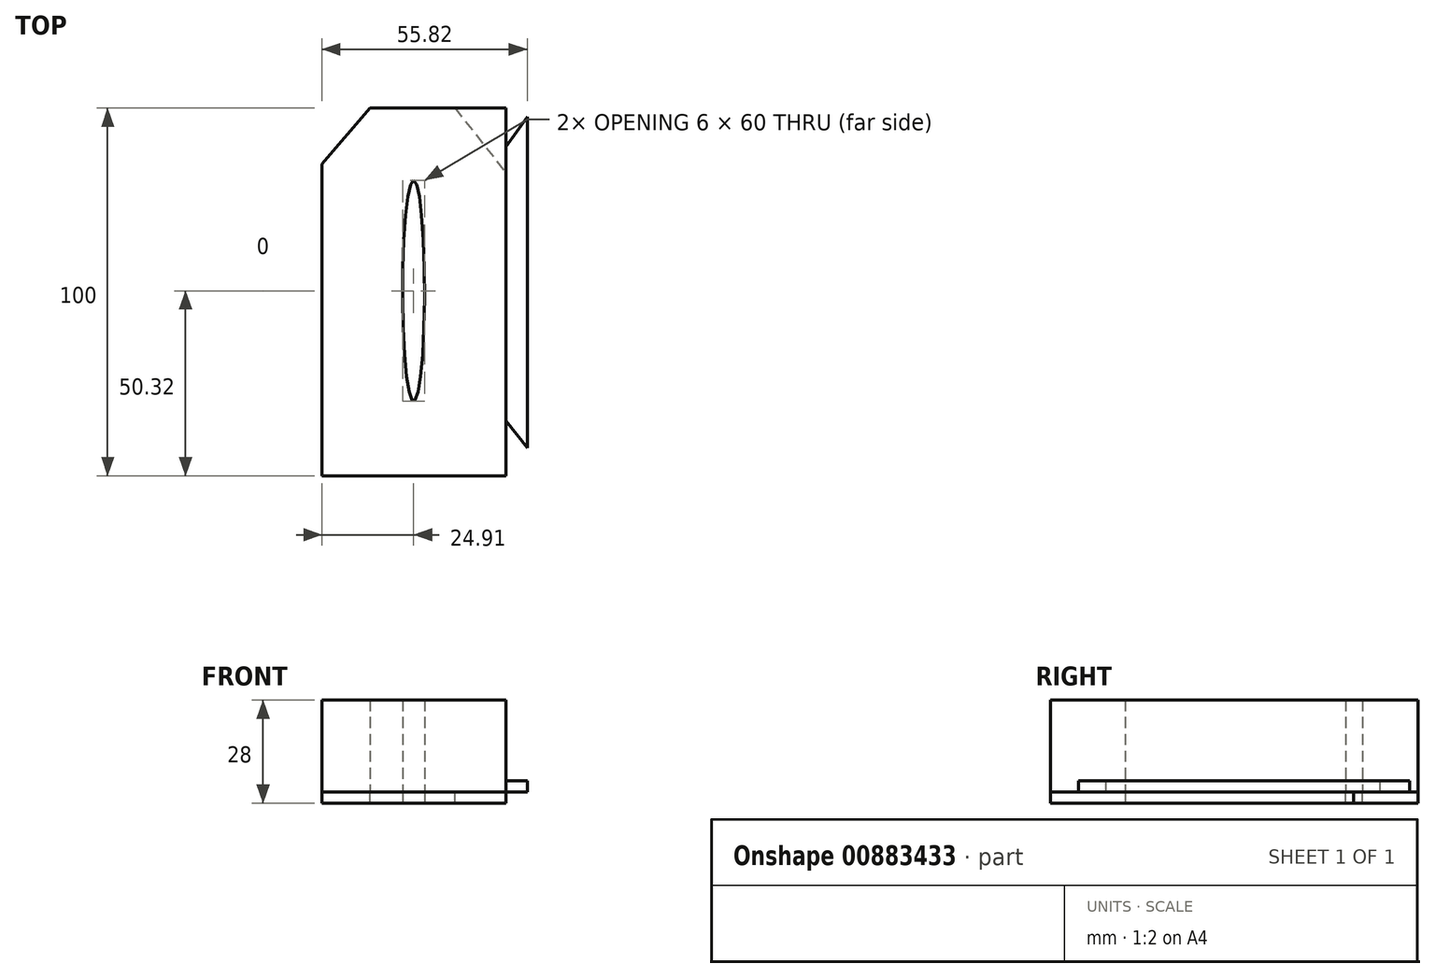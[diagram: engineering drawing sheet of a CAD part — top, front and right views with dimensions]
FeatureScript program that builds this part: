
annotation { "Feature Type Name" : "Feature", "Feature Type Description" : "" }
export const myFeature = defineFeature(function(context is Context, id is Id, definition is map)
    precondition{}
    {
        {
            var Q0;
            Q0=qCreatedBy(makeId("Top.planeOp"),FACE);
            var sketch = newSketch(context, id + "F0", { "sketchPlane" : qUnion([Q0])});
            skLineSegment(sketch, "E0.bottom", {"start": v(-24.91, 49.68) * mm, "end": v(25.09, 49.68) * mm});
            skLineSegment(sketch, "E0.top", {"start": v(-24.91, -50.32) * mm, "end": v(25.09, -50.32) * mm});
            skLineSegment(sketch, "E0.left", {"start": v(-24.91, 49.68) * mm, "end": v(-24.91, -50.32) * mm});
            skLineSegment(sketch, "E0.right", {"start": v(25.09, 49.68) * mm, "end": v(25.09, -50.32) * mm});
            skSolve(sketch);
        }
        {
            var Q0;
            Q0=makeQuery(id+"F0.imprint","IMPRINT",FACE,{"disambiguationData":[TD([[makeQuery(id+"F0.imprint","IMPRINT",EDGE,{"derivedFrom":sQuery(id+"F0.wireOp",EDGE,"E0.bottom")}),-1.0]])]});
            extrude(context, id + "F1", {"entities" : qUnion([Q0]), "depth" : 3 * mm, "offsetDistance" : 25 * mm});
        }
        {
            var Q0;
            Q0=makeQuery(id+"F1.opExtrude","CAP_FACE",FACE,{"disambiguationData":[OSD([sQuery(id+"F0.wireOp",EDGE,"E0.bottom"),sQuery(id+"F0.wireOp",EDGE,"E0.top"),sQuery(id+"F0.wireOp",EDGE,"E0.left"),sQuery(id+"F0.wireOp",EDGE,"E0.right")])],"isStart":false});
            var sketch = newSketch(context, id + "F2", { "sketchPlane" : qUnion([Q0])});
            skLineSegment(sketch, "E1", {"start": v(25.09, 39.2) * mm, "end": v(30.9, 47.34) * mm});
            skLineSegment(sketch, "E2", {"start": v(30.9, 47.34) * mm, "end": v(30.9, -42.66) * mm});
            skLineSegment(sketch, "E3", {"start": v(30.9, -42.66) * mm, "end": v(25.09, -35.3) * mm});
            skSolve(sketch);
        }
        {
            var Q0;
            {var subQ0=sQuery(id+"F2.wireOp",EDGE,"E1");Q0=makeQuery(id+"F2.imprint","IMPRINT",FACE,{"disambiguationData":[TD([[makeQuery(id+"F2.imprint","IMPRINT",EDGE,{"derivedFrom":subQ0}),-1.0]])]});}
            extrude(context, id + "F3", {"entities" : qUnion([Q0]), "depth" : 3 * mm, "offsetDistance" : 25 * mm});
        }
        {
            var Q0;
            Q0=makeQuery(id+"F1.opExtrude","CAP_FACE",FACE,{"disambiguationData":[OSD([sQuery(id+"F0.wireOp",EDGE,"E0.bottom"),sQuery(id+"F0.wireOp",EDGE,"E0.top"),sQuery(id+"F0.wireOp",EDGE,"E0.left"),sQuery(id+"F0.wireOp",EDGE,"E0.right")])],"isStart":false});
            var sketch = newSketch(context, id + "F4", { "sketchPlane" : qUnion([Q0])});
            skLineSegment(sketch, "E4", {"start": v(-24.91, 34.5) * mm, "end": v(-11.88, 49.68) * mm});
            skSolve(sketch);
        }
        {
            var Q0;
            {var subQ2=sQuery(id+"F4.wireOp",EDGE,"E4");Q0=makeQuery(id+"F4.imprint","IMPRINT",FACE,{"disambiguationData":[TD([[makeQuery(id+"F4.imprint","IMPRINT",EDGE,{"derivedFrom":subQ2}),-1.0]])]});}
            var sketch = newSketch(context, id + "F5", { "sketchPlane" : qUnion([Q0])});
            skLineSegment(sketch, "E5", {"start": v(12.58, 49.08) * mm, "end": v(24.3, 34.92) * mm});
            skSolve(sketch);
        }
        {
            var Q0;
            Q0 = qSketchRegion(id + "F4", true);
            var Q1;
            {var subQ0=sQuery(id+"F4.wireOp",EDGE,"E4");Q1=makeQuery(id+"F4.imprint","IMPRINT",FACE,{"disambiguationData":[TD([[makeQuery(id+"F4.imprint","IMPRINT",EDGE,{"derivedFrom":subQ0}),1.0]])]});}
            extrude(context, id + "F6", {"entities" : qUnion([Q0, Q1]), "operationType" : NewBodyOperationType.REMOVE, "oppositeDirection" : true, "depth" : 3 * mm, "offsetDistance" : 25 * mm});
        }
        {
            var Q0;
            {var subQ2=sQuery(id+"F4.wireOp",EDGE,"E4");Q0=makeQuery(id+"F5.imprint","IMPRINT",FACE,{"disambiguationData":[TD([[makeQuery(id+"F5.imprint","IMPRINT",EDGE,{"derivedFrom":makeQuery(id+"F4.imprint","IMPRINT",EDGE,{"derivedFrom":subQ2})}),-1.0]])]});}
            var sketch = newSketch(context, id + "F7", { "sketchPlane" : qUnion([Q0])});
            skLineSegment(sketch, "E6", {"start": v(11.05, 49.93) * mm, "end": v(25.51, 31.56) * mm});
            skSolve(sketch);
        }
        {
            var Q0;
            {var subQ0=sQuery(id+"F7.wireOp",EDGE,"E6");var subQ1=makeQuery(id+"F1.opExtrude","CAP_EDGE",EDGE,{"disambiguationData":[OSD([sQuery(id+"F0.wireOp",EDGE,"E0.right")])],"isStart":false});var subQ2=makeQuery(id+"F5.imprint","IMPRINT",EDGE,{"derivedFrom":makeQuery(id+"F4.imprint","IMPRINT",EDGE,{"derivedFrom":subQ1})});var subQ3=makeQuery(id+"F7.imprint","INTERSECT",VERTEX,{"derivedFrom":[subQ2,subQ0]});Q0=makeQuery(id+"F7.imprint","IMPRINT",FACE,{"disambiguationData":[TD([[makeQuery(id+"F7.imprint","IMPRINT",EDGE,{"disambiguationData":[TD([[subQ3,1.0]])],"derivedFrom":subQ0}),1.0]])]});}
            extrude(context, id + "F8", {"entities" : qUnion([Q0]), "operationType" : NewBodyOperationType.REMOVE, "oppositeDirection" : true, "depth" : 25 * mm, "offsetDistance" : 25 * mm});
        }
        {
            var Q0;
            {var subQ2=sQuery(id+"F4.wireOp",EDGE,"E4");Q0=makeQuery(id+"F5.imprint","IMPRINT",FACE,{"disambiguationData":[TD([[makeQuery(id+"F5.imprint","IMPRINT",EDGE,{"derivedFrom":makeQuery(id+"F4.imprint","IMPRINT",EDGE,{"derivedFrom":subQ2})}),-1.0]])]});}
            var sketch = newSketch(context, id + "F9", { "sketchPlane" : qUnion([Q0])});
            skSolve(sketch);
        }
        {
            var Q0;
            {var subQ2=sQuery(id+"F4.wireOp",EDGE,"E4");Q0=makeQuery(id+"F9.imprint","IMPRINT",FACE,{"disambiguationData":[TD([[makeQuery(id+"F9.imprint","IMPRINT",EDGE,{"derivedFrom":makeQuery(id+"F5.imprint","IMPRINT",EDGE,{"derivedFrom":makeQuery(id+"F4.imprint","IMPRINT",EDGE,{"derivedFrom":subQ2})})}),-1.0]])]});}
            var sketch = newSketch(context, id + "F10", { "sketchPlane" : qUnion([Q0])});
            skEllipse(sketch, "E7", {"center": v(0, 0) * mm, "majorRadius": 30 * mm, "minorRadius": 3 * mm, "majorAxis": v(0, 1)});
            skSolve(sketch);
        }
        {
            var Q0;
            Q0 = qSketchRegion(id + "F10", true);
            extrude(context, id + "F11", {"entities" : qUnion([Q0]), "operationType" : NewBodyOperationType.REMOVE, "oppositeDirection" : true, "depth" : 25 * mm, "offsetDistance" : 25 * mm});
        }
        {
            var Q0;
            Q0 = qSketchRegion(id + "F10", true);
            var Q1;
            {var subQ2=sQuery(id+"F4.wireOp",EDGE,"E4");Q1=makeQuery(id+"F9.imprint","IMPRINT",FACE,{"disambiguationData":[TD([[makeQuery(id+"F9.imprint","IMPRINT",EDGE,{"derivedFrom":makeQuery(id+"F5.imprint","IMPRINT",EDGE,{"derivedFrom":makeQuery(id+"F4.imprint","IMPRINT",EDGE,{"derivedFrom":subQ2})})}),-1.0]])]});}
            extrude(context, id + "F12", {"entities" : qUnion([Q0, Q1]), "depth" : 25 * mm, "offsetDistance" : 25 * mm});
        }
    });
